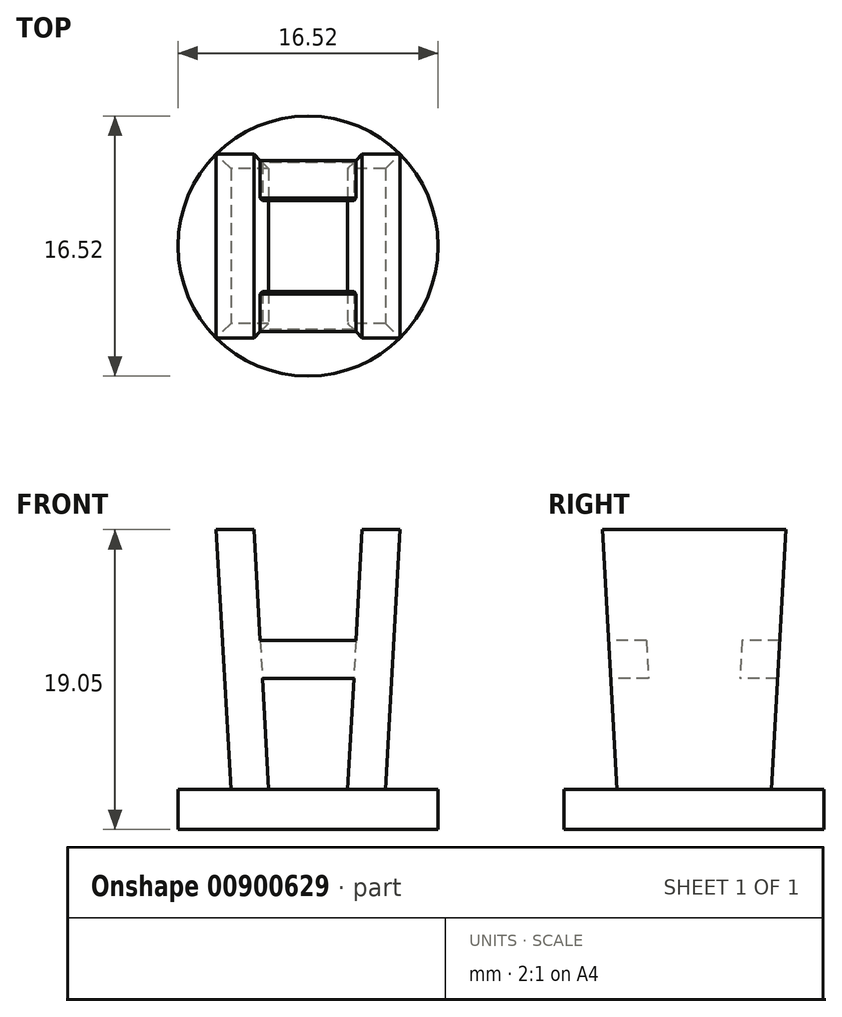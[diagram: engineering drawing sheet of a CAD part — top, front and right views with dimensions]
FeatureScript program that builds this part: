
annotation { "Feature Type Name" : "Feature", "Feature Type Description" : "" }
export const myFeature = defineFeature(function(context is Context, id is Id, definition is map)
    precondition{}
    {
        {
            var Q0;
            Q0=qCreatedBy(makeId("Top.planeOp"),FACE);
            var sketch = newSketch(context, id + "F0", { "sketchPlane" : qUnion([Q0])});
            skCircle(sketch, "E0", {"center": v(0, 0) * mm, "radius": 8.26 * mm});
            skSolve(sketch);
        }
        {
            var Q0;
            Q0=qSketchRegion(id+"F0",true);
            extrude(context, id + "F1", {"entities" : qUnion([Q0]), "depth" : 2.54 * mm, "offsetDistance" : 25.4 * mm});
        }
        {
            var Q0;
            Q0=qCreatedBy(makeId("Top.planeOp"),FACE);
            var sketch = newSketch(context, id + "F2", { "sketchPlane" : qUnion([Q0])});
            skLineSegment(sketch, "E1.bottom", {"start": v(4.76, 4.76) * mm, "end": v(-4.76, 4.76) * mm});
            skLineSegment(sketch, "E1.top", {"start": v(4.76, -4.76) * mm, "end": v(-4.76, -4.76) * mm});
            skLineSegment(sketch, "E1.left", {"start": v(4.76, 4.76) * mm, "end": v(4.76, -4.76) * mm});
            skLineSegment(sketch, "E1.right", {"start": v(-4.76, 4.76) * mm, "end": v(-4.76, -4.76) * mm});
            skPoint(sketch, "E1.middle", {"position": v(0, 0) * mm});
            skLineSegment(sketch, "E2.bottom", {"start": v(-4.76, 4.76) * mm, "end": v(-2.36, 4.76) * mm});
            skLineSegment(sketch, "E2.top", {"start": v(-4.76, 2.36) * mm, "end": v(-2.36, 2.36) * mm});
            skLineSegment(sketch, "E2.left", {"start": v(-4.76, 4.76) * mm, "end": v(-4.76, 2.36) * mm});
            skLineSegment(sketch, "E2.right", {"start": v(-2.36, 4.76) * mm, "end": v(-2.36, 2.36) * mm, "construction": true});
            skLineSegment(sketch, "E3.bottom", {"start": v(4.76, 4.76) * mm, "end": v(2.36, 4.76) * mm});
            skLineSegment(sketch, "E3.top", {"start": v(4.76, 2.36) * mm, "end": v(2.36, 2.36) * mm, "construction": true});
            skLineSegment(sketch, "E3.left", {"start": v(4.76, 4.76) * mm, "end": v(4.76, 2.36) * mm});
            skLineSegment(sketch, "E3.right", {"start": v(2.36, 4.76) * mm, "end": v(2.36, 2.36) * mm, "construction": true});
            skLineSegment(sketch, "E4.bottom", {"start": v(4.76, -4.76) * mm, "end": v(2.36, -4.76) * mm});
            skLineSegment(sketch, "E4.top", {"start": v(4.76, -2.36) * mm, "end": v(2.36, -2.36) * mm, "construction": true});
            skLineSegment(sketch, "E4.left", {"start": v(4.76, -4.76) * mm, "end": v(4.76, -2.36) * mm});
            skLineSegment(sketch, "E4.right", {"start": v(2.36, -4.76) * mm, "end": v(2.36, -2.36) * mm, "construction": true});
            skLineSegment(sketch, "E5.bottom", {"start": v(-4.76, -4.76) * mm, "end": v(-2.36, -4.76) * mm});
            skLineSegment(sketch, "E5.top", {"start": v(-4.76, -2.36) * mm, "end": v(-2.36, -2.36) * mm, "construction": true});
            skLineSegment(sketch, "E5.left", {"start": v(-4.76, -4.76) * mm, "end": v(-4.76, -2.36) * mm});
            skLineSegment(sketch, "E5.right", {"start": v(-2.36, -4.76) * mm, "end": v(-2.36, -2.36) * mm, "construction": true});
            skSolve(sketch);
        }
        {
            var Q0;
            Q0=qCreatedBy(makeId("Top.planeOp"),FACE);
            cPlane(context, id + "F3", {"entities" : qUnion([Q0]), "cplaneType" : CPlaneType.OFFSET, "offset" : 19.05 * mm, "width" : 152.4 * mm, "height" : 152.4 * mm});
        }
        {
            var Q0;
            Q0=qCreatedBy(id+"F3.planeOp",FACE);
            var sketch = newSketch(context, id + "F4", { "sketchPlane" : qUnion([Q0])});
            skLineSegment(sketch, "E6.bottom", {"start": v(-5.84, 5.84) * mm, "end": v(5.84, 5.84) * mm});
            skLineSegment(sketch, "E6.top", {"start": v(-5.84, -5.84) * mm, "end": v(5.84, -5.84) * mm});
            skLineSegment(sketch, "E6.left", {"start": v(-5.84, 5.84) * mm, "end": v(-5.84, -5.84) * mm});
            skLineSegment(sketch, "E6.right", {"start": v(5.84, 5.84) * mm, "end": v(5.84, -5.84) * mm});
            skPoint(sketch, "E6.middle", {"position": v(0, 0) * mm});
            skLineSegment(sketch, "E7.bottom", {"start": v(-5.84, 5.84) * mm, "end": v(-3.44, 5.84) * mm});
            skLineSegment(sketch, "E7.top", {"start": v(-5.84, 3.44) * mm, "end": v(-3.44, 3.44) * mm, "construction": true});
            skLineSegment(sketch, "E7.left", {"start": v(-5.84, 5.84) * mm, "end": v(-5.84, 3.44) * mm});
            skLineSegment(sketch, "E7.right", {"start": v(-3.44, 5.84) * mm, "end": v(-3.44, 3.44) * mm, "construction": true});
            skLineSegment(sketch, "E8.bottom", {"start": v(5.84, 5.84) * mm, "end": v(3.44, 5.84) * mm});
            skLineSegment(sketch, "E8.top", {"start": v(5.84, 3.44) * mm, "end": v(3.44, 3.44) * mm, "construction": true});
            skLineSegment(sketch, "E8.left", {"start": v(5.84, 5.84) * mm, "end": v(5.84, 3.44) * mm});
            skLineSegment(sketch, "E8.right", {"start": v(3.44, 5.84) * mm, "end": v(3.44, 3.44) * mm, "construction": true});
            skLineSegment(sketch, "E9.bottom", {"start": v(5.84, -5.84) * mm, "end": v(3.44, -5.84) * mm});
            skLineSegment(sketch, "E9.top", {"start": v(5.84, -3.44) * mm, "end": v(3.44, -3.44) * mm, "construction": true});
            skLineSegment(sketch, "E9.left", {"start": v(5.84, -5.84) * mm, "end": v(5.84, -3.44) * mm});
            skLineSegment(sketch, "E9.right", {"start": v(3.44, -5.84) * mm, "end": v(3.44, -3.44) * mm, "construction": true});
            skLineSegment(sketch, "E10.bottom", {"start": v(-5.84, -5.84) * mm, "end": v(-3.44, -5.84) * mm});
            skLineSegment(sketch, "E10.top", {"start": v(-5.84, -3.44) * mm, "end": v(-3.44, -3.44) * mm, "construction": true});
            skLineSegment(sketch, "E10.left", {"start": v(-5.84, -5.84) * mm, "end": v(-5.84, -3.44) * mm});
            skLineSegment(sketch, "E10.right", {"start": v(-3.44, -5.84) * mm, "end": v(-3.44, -3.44) * mm, "construction": true});
            skSolve(sketch);
        }
        {
            var Q1;
            Q1=makeQuery(id+"F2.imprint","IMPRINT",FACE,{"disambiguationData":[TD([[makeQuery(id+"F2.imprint","IMPRINT",EDGE,{"derivedFrom":sQuery(id+"F2.wireOp",EDGE,"E1.bottom")}),1.0]])]});
            var Q2;
            Q2=makeQuery(id+"F4.imprint","IMPRINT",FACE,{"disambiguationData":[TD([[makeQuery(id+"F4.imprint","IMPRINT",EDGE,{"derivedFrom":sQuery(id+"F4.wireOp",EDGE,"E6.bottom")}),-1.0]])]});
            loft(context, id + "F5", {"operationType" : NewBodyOperationType.ADD, "sheetProfilesArray" : [{ "sheetProfileEntities" : qUnion([Q1]) }, { "sheetProfileEntities" : qUnion([Q2]) }]});
        }
        {
            var Q0;
            Q0=qCreatedBy(makeId("Front.planeOp"),FACE);
            cPlane(context, id + "F6", {"entities" : qUnion([Q0]), "cplaneType" : CPlaneType.OFFSET, "offset" : 25.4 * mm, "width" : 152.4 * mm, "height" : 152.4 * mm});
        }
        {
            var Q0;
            Q0=qCreatedBy(id+"F6.planeOp",FACE);
            var sketch = newSketch(context, id + "F7", { "sketchPlane" : qUnion([Q0])});
            skLineSegment(sketch, "E11.0", {"start": v(4.9, 2.54) * mm, "end": v(5.84, 19.05) * mm});
            skLineSegment(sketch, "E11.1", {"start": v(-4.9, 2.54) * mm, "end": v(-5.84, 19.05) * mm});
            skLineSegment(sketch, "E11.2", {"start": v(4.9, 2.54) * mm, "end": v(-4.9, 2.54) * mm});
            skLineSegment(sketch, "E11.3", {"start": v(-5.84, 19.05) * mm, "end": v(5.84, 19.05) * mm});
            skLineSegment(sketch, "E12", {"start": v(3.44, 19.05) * mm, "end": v(2.5, 2.54) * mm});
            skLineSegment(sketch, "E13", {"start": v(-3.44, 19.05) * mm, "end": v(-2.5, 2.54) * mm});
            skLineSegment(sketch, "E14", {"start": v(5.37, 10.8) * mm, "end": v(-5.37, 10.8) * mm, "construction": true});
            skLineSegment(sketch, "E15", {"start": v(3.04, 12) * mm, "end": v(-3.04, 12) * mm});
            skLineSegment(sketch, "E16", {"start": v(-2.9, 9.6) * mm, "end": v(2.9, 9.6) * mm});
            skLineSegment(sketch, "E17", {"start": v(0, 12) * mm, "end": v(0, 9.6) * mm, "construction": true});
            skPoint(sketch, "E18", {"position": v(0, 10.8) * mm});
            skSolve(sketch);
        }
        {
            var Q0;
            {var subQ5=sQuery(id+"F7.wireOp",EDGE,"E15");Q0=makeQuery(id+"F7.imprint","IMPRINT",FACE,{"disambiguationData":[TD([[makeQuery(id+"F7.imprint","IMPRINT",EDGE,{"derivedFrom":subQ5}),-1.0]])]});}
            var Q1;
            {var subQ5=sQuery(id+"F7.wireOp",EDGE,"E16");Q1=makeQuery(id+"F7.imprint","IMPRINT",FACE,{"disambiguationData":[TD([[makeQuery(id+"F7.imprint","IMPRINT",EDGE,{"derivedFrom":subQ5}),-1.0]])]});}
            extrude(context, id + "F8", {"entities" : qUnion([Q0, Q1]), "operationType" : NewBodyOperationType.REMOVE, "endBound" : BoundingType.THROUGH_ALL, "oppositeDirection" : true, "depth" : 25.4 * mm, "offsetDistance" : 25.4 * mm});
        }
        {
            var Q0;
            {var subQ0=sQuery(id+"F7.wireOp",EDGE,"E15");Q0=makeQuery(id+"FSzBBtu7wnrdoTO_1.1.F8.boolean.opBoolean","MERGE",FACE,{"derivedFrom":[makeQuery(id+"F8.boolean.opBoolean","COPY",FACE,{"derivedFrom":makeQuery(id+"F8.opExtrude","SWEPT_FACE",FACE,{"disambiguationData":[OSD([subQ0])]})})],"fromTools":[makeQuery(id+"FSzBBtu7wnrdoTO_1.1.F8.opExtrude","SWEPT_FACE",FACE,{"disambiguationData":[OSD([subQ0])]})]});}
            var sketch = newSketch(context, id + "F9", { "sketchPlane" : qUnion([Q0])});
            skLineSegment(sketch, "E19.bottom", {"start": v(-3.04, 3.04) * mm, "end": v(3.04, 3.04) * mm});
            skLineSegment(sketch, "E19.top", {"start": v(-3.04, -3.04) * mm, "end": v(3.04, -3.04) * mm});
            skLineSegment(sketch, "E19.left", {"start": v(-3.04, 3.04) * mm, "end": v(-3.04, -3.04) * mm});
            skLineSegment(sketch, "E19.right", {"start": v(3.04, 3.04) * mm, "end": v(3.04, -3.04) * mm});
            skSolve(sketch);
        }
        {
            var Q0;
            {var subQ0=sQuery(id+"F7.wireOp",EDGE,"E16");Q0=makeQuery(id+"FSzBBtu7wnrdoTO_1.1.F8.boolean.opBoolean","MERGE",FACE,{"derivedFrom":[makeQuery(id+"F8.boolean.opBoolean","COPY",FACE,{"derivedFrom":makeQuery(id+"F8.opExtrude","SWEPT_FACE",FACE,{"disambiguationData":[OSD([subQ0])]})})],"fromTools":[makeQuery(id+"FSzBBtu7wnrdoTO_1.1.F8.opExtrude","SWEPT_FACE",FACE,{"disambiguationData":[OSD([subQ0])]})]});}
            var sketch = newSketch(context, id + "F10", { "sketchPlane" : qUnion([Q0])});
            skLineSegment(sketch, "E20.bottom", {"start": v(-2.9, 2.9) * mm, "end": v(2.9, 2.9) * mm});
            skLineSegment(sketch, "E20.top", {"start": v(-2.9, -2.9) * mm, "end": v(2.9, -2.9) * mm});
            skLineSegment(sketch, "E20.left", {"start": v(-2.9, 2.9) * mm, "end": v(-2.9, -2.9) * mm});
            skLineSegment(sketch, "E20.right", {"start": v(2.9, 2.9) * mm, "end": v(2.9, -2.9) * mm});
            skSolve(sketch);
        }
        {
            var Q1;
            Q1=qSketchRegion(id+"F9",true);
            var Q2;
            Q2=qSketchRegion(id+"F10",true);
            loft(context, id + "F11", {"operationType" : NewBodyOperationType.REMOVE, "sheetProfilesArray" : [{ "sheetProfileEntities" : qUnion([Q1]) }, { "sheetProfileEntities" : qUnion([Q2]) }]});
        }
    });
